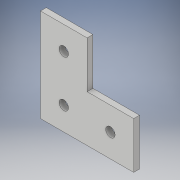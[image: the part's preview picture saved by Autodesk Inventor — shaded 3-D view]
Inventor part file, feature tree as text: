
AUTODESK INVENTOR PART (.ipt)
format: ipt  version: 2018 (Build 220112000, 112)  size: 108,544 bytes
history: native  units: in
note: dims shown in document units (in); Inventor stores cm internally (conversion verified against a paired STEP export)
features: extrude x1, sketch x1
ambient origin geometry x8: Origin, YZ Plane, XZ Plane, XY Plane, X Axis, Y Axis, Z Axis, Center Point
bodies: Solid1 (feature_tree), Body1 (feature_tree)
feature tree (2):
  extrude  "Extrusion1"  Depth=1.0in
  sketch  "Sketch1"  dims[d0=1.0in d1=1.0in d2=1.0in d3=0.0in]
